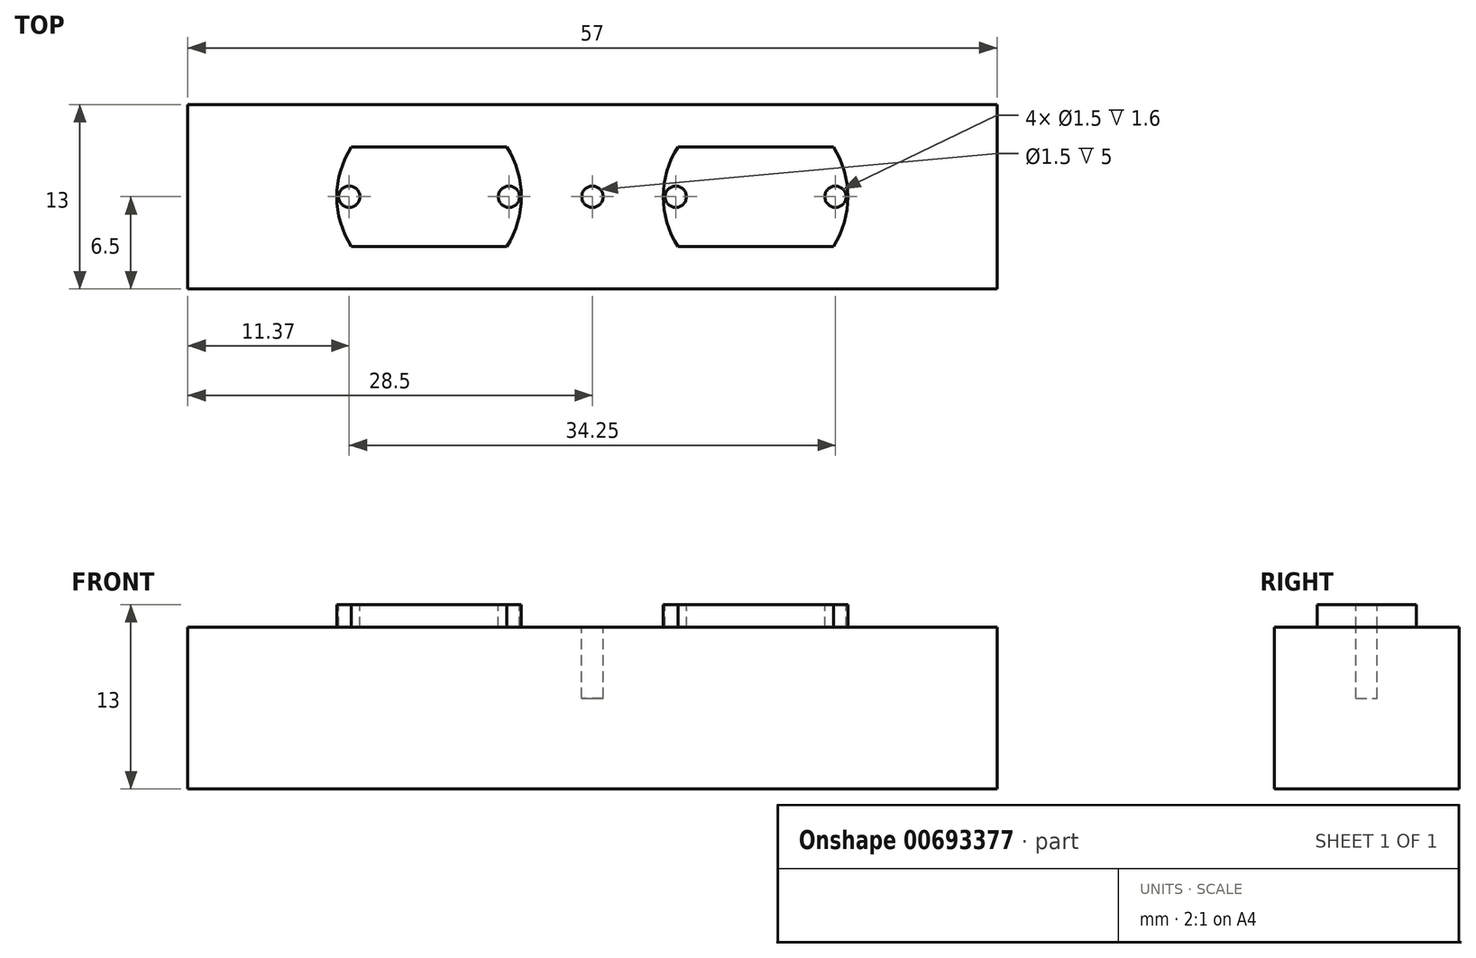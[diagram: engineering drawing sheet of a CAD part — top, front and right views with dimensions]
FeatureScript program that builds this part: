
annotation { "Feature Type Name" : "Feature", "Feature Type Description" : "" }
export const myFeature = defineFeature(function(context is Context, id is Id, definition is map)
    precondition{}
    {
        {
            var Q0;
            Q0=qCreatedBy(makeId("Top.planeOp"),FACE);
            var sketch = newSketch(context, id + "F0", { "sketchPlane" : qUnion([Q0])});
            skLineSegment(sketch, "E0.bottom", {"start": v(-28.5, 6.5) * mm, "end": v(28.5, 6.5) * mm});
            skLineSegment(sketch, "E0.top", {"start": v(-28.5, -6.5) * mm, "end": v(28.5, -6.5) * mm});
            skLineSegment(sketch, "E0.left", {"start": v(-28.5, 6.5) * mm, "end": v(-28.5, -6.5) * mm});
            skLineSegment(sketch, "E0.right", {"start": v(28.5, 6.5) * mm, "end": v(28.5, -6.5) * mm});
            skSolve(sketch);
        }
        {
            var Q0;
            Q0=makeQuery(id+"F0.imprint","IMPRINT",FACE,{"disambiguationData":[TD([[makeQuery(id+"F0.imprint","IMPRINT",EDGE,{"derivedFrom":sQuery(id+"F0.wireOp",EDGE,"E0.bottom")}),-1.0]])]});
            extrude(context, id + "F1", {"entities" : qUnion([Q0]), "depth" : 13 * mm, "offsetDistance" : 25 * mm});
        }
        {
            var Q0;
            Q0=makeQuery(id+"F1.opExtrude","CAP_FACE",FACE,{"disambiguationData":[OSD([sQuery(id+"F0.wireOp",EDGE,"E0.bottom"),sQuery(id+"F0.wireOp",EDGE,"E0.top"),sQuery(id+"F0.wireOp",EDGE,"E0.left"),sQuery(id+"F0.wireOp",EDGE,"E0.right")])],"isStart":false});
            var sketch = newSketch(context, id + "F2", { "sketchPlane" : qUnion([Q0])});
            skArc(sketch, "E1", {"start": v(-6.03, -3.5) * mm, "mid": v(-5, 0) * mm, "end": v(-6.03, 3.5) * mm});
            skArc(sketch, "E2", {"start": v(6.02, 3.5) * mm, "mid": v(5, 0) * mm, "end": v(6.02, -3.5) * mm});
            skCircle(sketch, "E3", {"center": v(-17.13, 0) * mm, "radius": 0.75 * mm});
            skCircle(sketch, "E4", {"center": v(-5.88, 0) * mm, "radius": 0.75 * mm});
            skCircle(sketch, "E5", {"center": v(5.87, 0) * mm, "radius": 0.75 * mm});
            skCircle(sketch, "E6", {"center": v(17.12, 0) * mm, "radius": 0.75 * mm});
            skLineSegment(sketch, "E7", {"start": v(-16.98, 3.5) * mm, "end": v(-6.03, 3.5) * mm});
            skLineSegment(sketch, "E8", {"start": v(-16.98, -3.5) * mm, "end": v(-6.03, -3.5) * mm});
            skLineSegment(sketch, "E9.trimOffspring", {"start": v(6.02, 3.5) * mm, "end": v(16.97, 3.5) * mm});
            skLineSegment(sketch, "E10.trimOffspring", {"start": v(6.02, -3.5) * mm, "end": v(16.97, -3.5) * mm});
            skArc(sketch, "E11.trimOffspring", {"start": v(-16.98, 3.5) * mm, "mid": v(-18, 0) * mm, "end": v(-16.98, -3.5) * mm});
            skArc(sketch, "E12.trimOffspring", {"start": v(16.97, -3.5) * mm, "mid": v(18, 0) * mm, "end": v(16.97, 3.5) * mm});
            skSolve(sketch);
        }
        {
            var Q0;
            Q0=makeQuery(id+"F2.imprint","IMPRINT",FACE,{"disambiguationData":[TD([[makeQuery(id+"F2.imprint","IMPRINT",EDGE,{"derivedFrom":sQuery(id+"F2.wireOp",EDGE,"E1")}),-1.0]])]});
            var Q1;
            Q1=makeQuery(id+"F2.imprint","IMPRINT",FACE,{"disambiguationData":[TD([[makeQuery(id+"F2.imprint","IMPRINT",EDGE,{"derivedFrom":sQuery(id+"F2.wireOp",EDGE,"E3")}),1.0]])]});
            var Q2;
            Q2=makeQuery(id+"F2.imprint","IMPRINT",FACE,{"disambiguationData":[TD([[makeQuery(id+"F2.imprint","IMPRINT",EDGE,{"derivedFrom":sQuery(id+"F2.wireOp",EDGE,"E4")}),1.0]])]});
            var Q3;
            Q3=makeQuery(id+"F2.imprint","IMPRINT",FACE,{"disambiguationData":[TD([[makeQuery(id+"F2.imprint","IMPRINT",EDGE,{"derivedFrom":sQuery(id+"F2.wireOp",EDGE,"E5")}),1.0]])]});
            var Q4;
            Q4=makeQuery(id+"F2.imprint","IMPRINT",FACE,{"disambiguationData":[TD([[makeQuery(id+"F2.imprint","IMPRINT",EDGE,{"derivedFrom":sQuery(id+"F2.wireOp",EDGE,"E6")}),1.0]])]});
            extrude(context, id + "F3", {"entities" : qUnion([Q0, Q1, Q2, Q3, Q4]), "operationType" : NewBodyOperationType.REMOVE, "oppositeDirection" : true, "depth" : 1.6 * mm, "offsetDistance" : 25 * mm});
        }
        {
            var Q0;
            Q0=makeQuery(id+"F1.opExtrude","SWEPT_BODY",BODY,{"disambiguationData":[OSD([sQuery(id+"F0.wireOp",EDGE,"E0.bottom"),sQuery(id+"F0.wireOp",EDGE,"E0.top"),sQuery(id+"F0.wireOp",EDGE,"E0.left"),sQuery(id+"F0.wireOp",EDGE,"E0.right")])]});
            var Q1;
            Q1=makeQuery(id+"F1.opExtrude","CAP_EDGE",EDGE,{"disambiguationData":[OSD([sQuery(id+"F0.wireOp",EDGE,"E0.bottom")])],"isStart":true});
            transform(context, id + "F4", {"entities" : qUnion([Q0]), "transformType" : TransformType.ROTATION, "transformAxis" : qUnion([Q1]), "angle" : 180 * degree, "oppositeDirection" : true, "makeCopy" : false});
        }
        {
            var Q0;
            Q0=makeQuery(id+"F1.opExtrude","SWEPT_BODY",BODY,{"disambiguationData":[OSD([sQuery(id+"F0.wireOp",EDGE,"E0.bottom"),sQuery(id+"F0.wireOp",EDGE,"E0.top"),sQuery(id+"F0.wireOp",EDGE,"E0.left"),sQuery(id+"F0.wireOp",EDGE,"E0.right")])]});
            var Q1;
            Q1=makeQuery(id+"F1.opExtrude","CAP_EDGE",EDGE,{"disambiguationData":[OSD([sQuery(id+"F0.wireOp",EDGE,"E0.bottom")])],"isStart":true});
            transform(context, id + "F5", {"entities" : qUnion([Q0]), "transformType" : TransformType.ROTATION, "transformAxis" : qUnion([Q1]), "angle" : 180 * degree, "oppositeDirection" : true, "makeCopy" : false});
        }
        {
            var Q0;
            Q0=makeQuery(id+"F3.boolean.opBoolean","COPY",FACE,{"derivedFrom":makeQuery(id+"F3.opExtrude","CAP_FACE",FACE,{"disambiguationData":[OSD([sQuery(id+"F0.wireOp",EDGE,"E0.bottom"),sQuery(id+"F0.wireOp",EDGE,"E0.top"),sQuery(id+"F0.wireOp",EDGE,"E0.left"),sQuery(id+"F0.wireOp",EDGE,"E0.right"),sQuery(id+"F2.wireOp",EDGE,"E1"),sQuery(id+"F2.wireOp",EDGE,"E2"),sQuery(id+"F2.wireOp",EDGE,"E7"),sQuery(id+"F2.wireOp",EDGE,"E8"),sQuery(id+"F2.wireOp",EDGE,"E9.trimOffspring"),sQuery(id+"F2.wireOp",EDGE,"E10.trimOffspring"),sQuery(id+"F2.wireOp",EDGE,"E11.trimOffspring"),sQuery(id+"F2.wireOp",EDGE,"E12.trimOffspring")])],"isStart":false})});
            var sketch = newSketch(context, id + "F6", { "sketchPlane" : qUnion([Q0])});
            skCircle(sketch, "E13", {"center": v(0, 0) * mm, "radius": 0.75 * mm});
            skSolve(sketch);
        }
        {
            var Q0;
            Q0=makeQuery(id+"F6.imprint","IMPRINT",FACE,{"disambiguationData":[TD([[makeQuery(id+"F6.imprint","IMPRINT",EDGE,{"derivedFrom":sQuery(id+"F6.wireOp",EDGE,"E13")}),1.0]])]});
            extrude(context, id + "F7", {"entities" : qUnion([Q0]), "operationType" : NewBodyOperationType.REMOVE, "oppositeDirection" : true, "depth" : (5) * mm, "offsetDistance" : 25 * mm});
        }
    });
